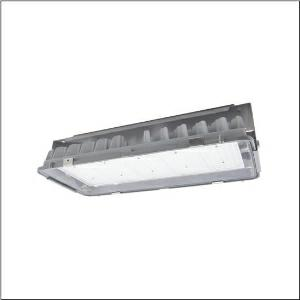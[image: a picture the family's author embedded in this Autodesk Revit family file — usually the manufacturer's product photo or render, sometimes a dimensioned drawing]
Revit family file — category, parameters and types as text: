
# Revit family: highbay_11xtreme_51hf82da4nma
name_source: partatom
category: Lighting Fixtures
units: mm (PartAtom-declared; Revit-internal decimal feet)

## family parameters
Cut with Voids When Loaded = No
Host = Face
Light Source = No
Part Type = Normal
Room Calculation Point = No
Round Connector Dimension = Use Diameter
Shared = No

## types (1)
- --- (1 x LED, 33700 lm, 187.7 W, 4000K)
    Apparent Load = 188 VA
    CIE Flux Codes = 84 96 100 100 100
    Color Rendering = 80
    Color Temperature = 4000K
    Default Elevation = 1800 mm
    Description = Highbay 11Xtreme, high bay luminaire, primary light control with lens, of PMMA, primary optical cover: cover, of toughened safety glass, light emission: direct distribution, primary light characteristic: symmetric, installation type: suspended mounting, surface-mounted, 1x LED module,for 1x LED, rated luminous flux: 33.700lm, luminous efficacy: 180lm/W, light colour: 840, colour temperature: 4000K, control gear: DALI 2, with cable H07RN-F 5x 1.5mm², mains connection: 220..240V, AC, 50/60Hz, cable length: 1,5m, rated input power: 188W, luminaire housing, of diecast aluminium, partly coated, silver, length: 595mm, width: 280mm, height: 195mm, protection rating (complete): IP66, insulation class (complete): insulation class I (protective earthing), certification: CE, ENEC, UKCA, protection symbol: D, ball protection: ball impact resistant according to DIN VDE 0710 part 13 (with chain suspension), impact resistance: IK08, permissible operating ambient temperature: -25..+45°C, reducing of maximum allowable ambient temperature of 5°C with ceiling mounting, packaging unit: 1 piece
    Height = 157 mm
    Lamp = 1 x LED
    Lamp Light Flux = 33700 lm
    Lamp Power = 187.7 W
    Lamp count = 1
    Length = 593 mm
    Luminous efficacy = 180 lm/W
    Manufacturer = Siteco
    ModVariant = No
    Model = 51HF82DA4NMA
    Mounting Place = Ceiling
    Mounting Type = Pendant
    Number of Poles = 1
    OnlyDefault = Yes
    Power Factor = 1
    Product Name = Highbay 11Xtreme
    Product group = high bay luminaire
    ProductGroupID = 901
    Protection Class = Protection class I
    Protection Degree = IP 66
    RLX_Detail_Level = 1
    RLX_Emergency_Light_Flux = 0 lm
    RLX_Emergency_Type = 0
    RLX_Emergency_Type_DB = No
    RlxData = <blob elided: 28377 chars, md5=6f0241a4>
    Socket = socket
    Standby Power = 0 W
    System Light Flux = 33700 lm
    System Power = 188 W
    Type Comments = factory setting: luminous flux: 100 % | dim-lin: 254 | 1255 mA
    Type Image = l_1258342.jpg
    URL = http://relux.com
    VarID = @adj_104669
    Voltage = 0 V
    Weight = 0.00 kg
    Width = 568 mm

## geometry (parser evidence)
native form markers: Blend x4, Sweep x9
no freeform markers — native parametric forms only
